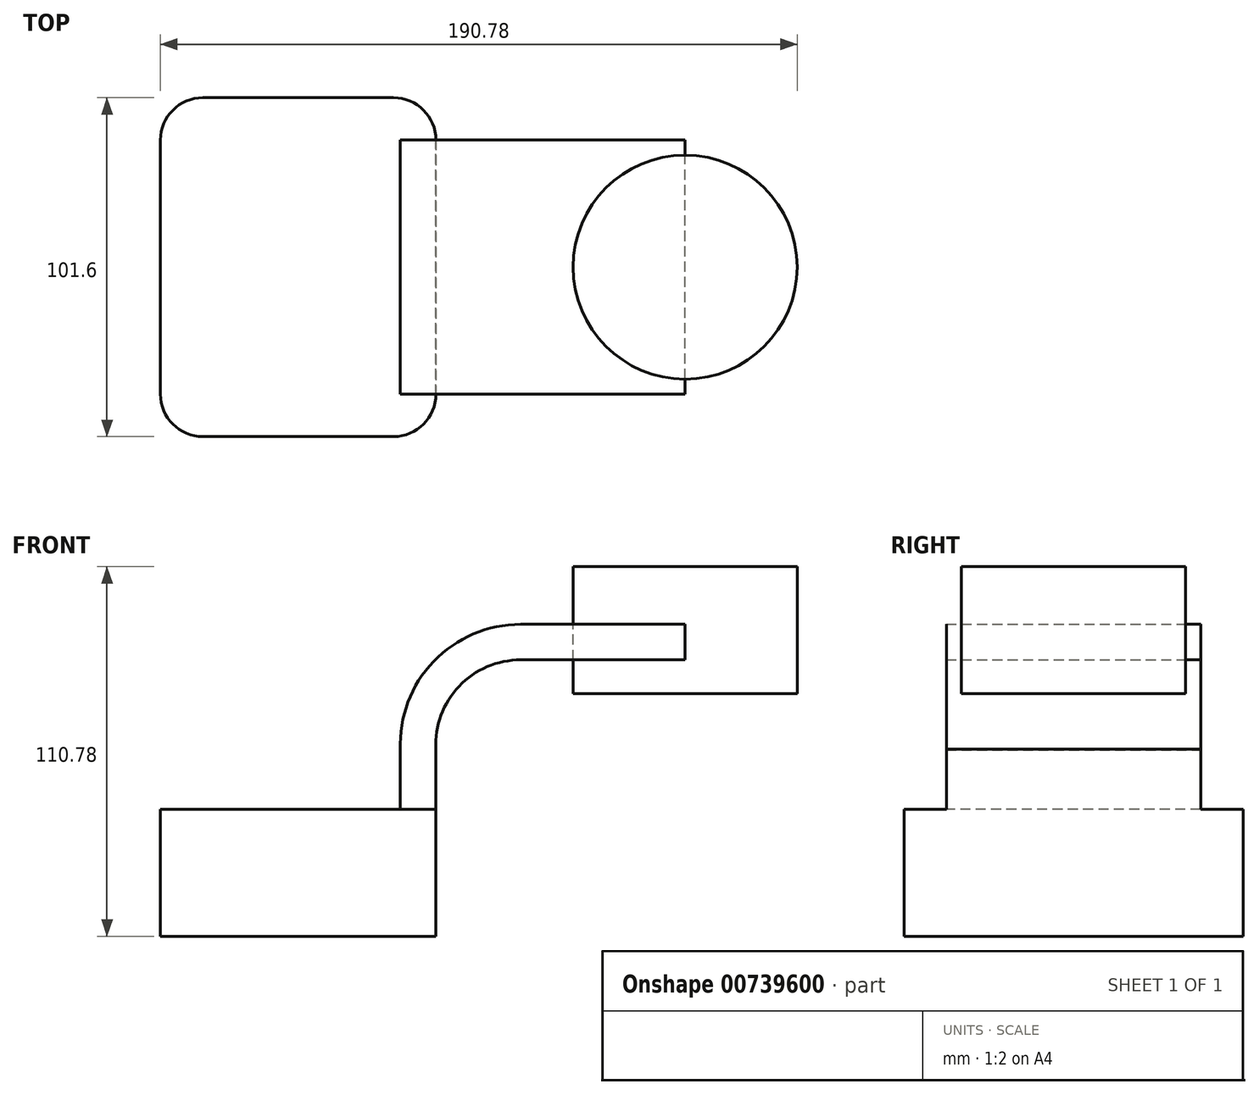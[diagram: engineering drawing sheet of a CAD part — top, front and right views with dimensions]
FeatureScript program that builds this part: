
annotation { "Feature Type Name" : "Feature", "Feature Type Description" : "" }
export const myFeature = defineFeature(function(context is Context, id is Id, definition is map)
    precondition{}
    {
        {
            var Q0;
            Q0=qCreatedBy(makeId("Front.planeOp"),FACE);
            var sketch = newSketch(context, id + "F0", { "sketchPlane" : qUnion([Q0])});
            skLineSegment(sketch, "E0.bottom", {"start": v(-41.28, 19.05) * mm, "end": v(41.28, 19.05) * mm});
            skLineSegment(sketch, "E0.top", {"start": v(-41.28, -19.05) * mm, "end": v(41.27, -19.05) * mm});
            skLineSegment(sketch, "E0.left", {"start": v(-41.28, 19.05) * mm, "end": v(-41.28, -19.05) * mm});
            skLineSegment(sketch, "E0.right", {"start": v(41.28, 19.05) * mm, "end": v(41.27, -19.05) * mm});
            skPoint(sketch, "E0.middle", {"position": v(0, 0) * mm});
            skLineSegment(sketch, "E1.bottom", {"start": v(98.71, 91.73) * mm, "end": v(149.51, 91.73) * mm});
            skLineSegment(sketch, "E1.top", {"start": v(98.71, 53.63) * mm, "end": v(149.51, 53.63) * mm});
            skLineSegment(sketch, "E1.left", {"start": v(98.71, 91.73) * mm, "end": v(98.71, 53.63) * mm});
            skLineSegment(sketch, "E1.right", {"start": v(149.51, 91.73) * mm, "end": v(149.51, 53.63) * mm});
            skPoint(sketch, "E1.middle", {"position": v(124.11, 72.68) * mm});
            skLineSegment(sketch, "E2", {"start": v(41.28, 19.05) * mm, "end": v(41.28, 37.07) * mm});
            skArc(sketch, "E3", {"start": v(41.28, 37.07) * mm, "mid": v(48.21, 55.89) * mm, "end": v(66.64, 63.8) * mm});
            skLineSegment(sketch, "E4", {"start": v(66.64, 63.8) * mm, "end": v(115.95, 63.8) * mm});
            skLineSegment(sketch, "E5.0", {"start": v(66.64, 74.47) * mm, "end": v(115.95, 74.47) * mm});
            skArc(sketch, "E5.1", {"start": v(30.6, 36.81) * mm, "mid": v(40.58, 63.34) * mm, "end": v(66.64, 74.47) * mm});
            skLineSegment(sketch, "E5.2", {"start": v(30.6, 19.05) * mm, "end": v(30.6, 36.81) * mm});
            skFitSpline(sketch, "E6", {"points": [v(-41.28, 19.05) * mm, v(66.64, 74.47) * mm], "startDerivative": vector(179.99, 14.45) * mm, "endDerivative": vector(123.12, -4.3) * mm});
            skLineSegment(sketch, "E7", {"start": v(115.95, 91.73) * mm, "end": v(115.95, 53.63) * mm});
            skSolve(sketch);
        }
        {
            var Q0;
            Q0=makeQuery(id+"F0.imprint","IMPRINT",FACE,{"disambiguationData":[TD([[makeQuery(id+"F0.imprint","IMPRINT",EDGE,{"derivedFrom":sQuery(id+"F0.wireOp",EDGE,"E0.top")}),1.0]])]});
            extrude(context, id + "F1", {"entities" : qUnion([Q0]), "endBound" : BoundingType.SYMMETRIC, "oppositeDirection" : true, "depth" : 101.6 * mm, "offsetDistance" : 25.4 * mm});
        }
        {
            var Q0;
            Q0=makeQuery(id+"F0.imprint","IMPRINT",FACE,{"disambiguationData":[TD([[makeQuery(id+"F0.imprint","IMPRINT",EDGE,{"derivedFrom":sQuery(id+"F0.wireOp",EDGE,"E5.1")}),1.0]])]});
            extrude(context, id + "F2", {"entities" : qUnion([Q0]), "operationType" : NewBodyOperationType.ADD, "endBound" : BoundingType.SYMMETRIC, "depth" : 25.4 * mm, "offsetDistance" : 25.4 * mm});
        }
        {
            var Q0;
            {var subQ1=sQuery(id+"F0.wireOp",EDGE,"E2");Q0=makeQuery(id+"F0.imprint","IMPRINT",FACE,{"disambiguationData":[TD([[makeQuery(id+"F0.imprint","IMPRINT",EDGE,{"derivedFrom":subQ1}),1.0]])]});}
            var Q1;
            {var subQ0=sQuery(id+"F0.wireOp",EDGE,"E5.0");var subQ1=sQuery(id+"F0.wireOp",EDGE,"E1.left");var subQ2=makeQuery(id+"F0.imprint","INTERSECT",VERTEX,{"derivedFrom":[subQ1,subQ0]});Q1=makeQuery(id+"F0.imprint","IMPRINT",FACE,{"disambiguationData":[TD([[makeQuery(id+"F0.imprint","IMPRINT",EDGE,{"disambiguationData":[TD([[subQ2,-1.0]])],"derivedFrom":subQ1}),1.0]])]});}
            extrude(context, id + "F3", {"entities" : qUnion([Q0, Q1]), "operationType" : NewBodyOperationType.ADD, "endBound" : BoundingType.SYMMETRIC, "depth" : 76.2 * mm, "offsetDistance" : 25.4 * mm});
        }
        {
            var Q0;
            {var subQ4=sQuery(id+"F0.wireOp",EDGE,"E1.right");Q0=makeQuery(id+"F0.imprint","IMPRINT",FACE,{"disambiguationData":[TD([[makeQuery(id+"F0.imprint","IMPRINT",EDGE,{"derivedFrom":subQ4}),-1.0]])]});}
            var Q1;
            Q1=sQuery(id+"F0.wireOp",EDGE,"E1.top");
            var Q2;
            Q2=sQuery(id+"F0.wireOp",EDGE,"E1.right");
            var Q3;
            Q3=sQuery(id+"F0.wireOp",EDGE,"E7");
            var Q4;
            Q4=sQuery(id+"F0.wireOp",EDGE,"E1.bottom");
            var Q5;
            Q5=sQuery(id+"F0.wireOp",EDGE,"E7");
            revolve(context, id + "F4", {"surfaceOperationType" : NewSurfaceOperationType.NEW, "entities" : qUnion([Q0]), "surfaceEntities" : qUnion([Q1, Q2, Q3, Q4]), "axis" : qUnion([Q5]), "revolveType" : RevolveType.FULL});
        }
        {
            var Q0;
            Q0=makeQuery(id+"F1.opExtrude","CAP_EDGE",EDGE,{"disambiguationData":[OSD([sQuery(id+"F0.wireOp",EDGE,"E0.right")])],"isStart":true});
            var Q1;
            Q1=makeQuery(id+"F1.opExtrude","CAP_EDGE",EDGE,{"disambiguationData":[OSD([sQuery(id+"F0.wireOp",EDGE,"E0.left")])],"isStart":true});
            var Q2;
            Q2=makeQuery(id+"F1.opExtrude","CAP_EDGE",EDGE,{"disambiguationData":[OSD([sQuery(id+"F0.wireOp",EDGE,"E0.right")])],"isStart":false});
            var Q3;
            Q3=makeQuery(id+"F1.opExtrude","CAP_EDGE",EDGE,{"disambiguationData":[OSD([sQuery(id+"F0.wireOp",EDGE,"E0.left")])],"isStart":false});
            fillet(context, id + "F5", {"entities" : qUnion([Q0, Q1, Q2, Q3]), "radius" : 12.7 * mm, "tangentPropagation" : true, "allowEdgeOverflow" : false});
        }
    });
